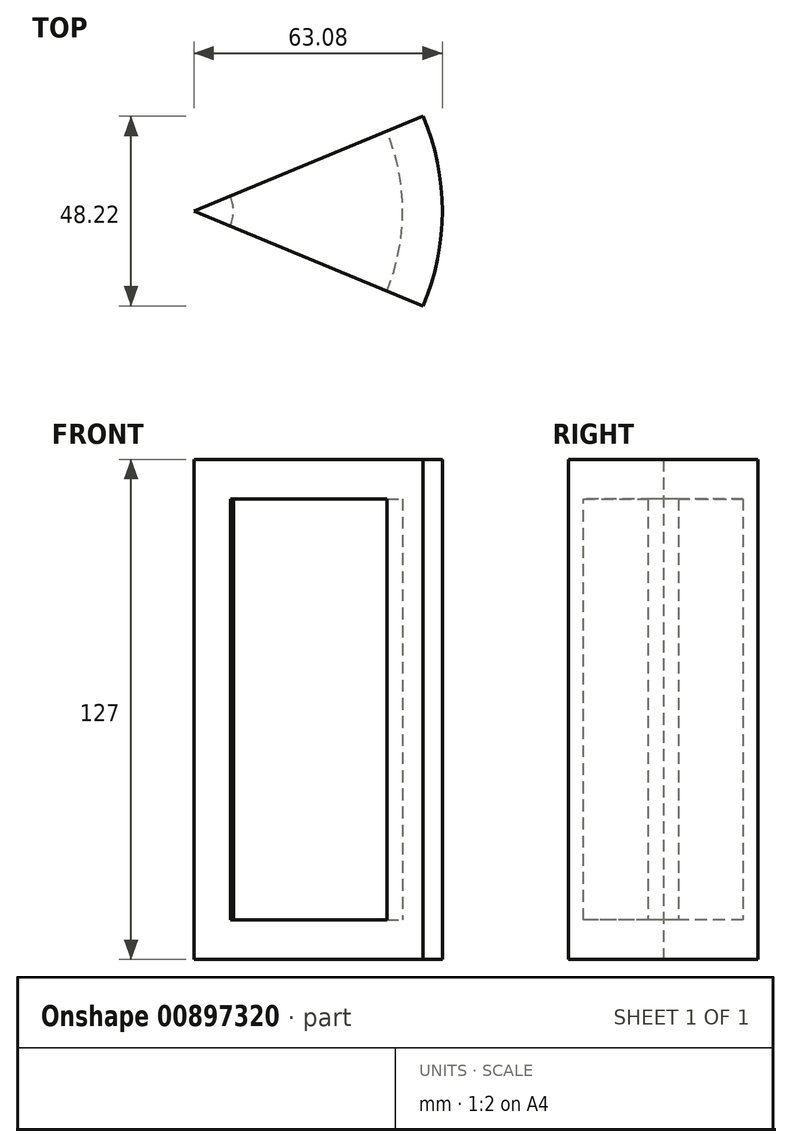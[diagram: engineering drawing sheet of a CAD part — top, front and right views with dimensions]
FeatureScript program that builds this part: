
annotation { "Feature Type Name" : "Feature", "Feature Type Description" : "" }
export const myFeature = defineFeature(function(context is Context, id is Id, definition is map)
    precondition{}
    {
        {
            var Q0;
            Q0=qCreatedBy(makeId("Top.planeOp"),FACE);
            var sketch = newSketch(context, id + "F0", { "sketchPlane" : qUnion([Q0])});
            skLineSegment(sketch, "E0", {"start": v(0, 0) * mm, "end": v(58.2, 24.1) * mm});
            skLineSegment(sketch, "E1", {"start": v(0, 0) * mm, "end": v(58.2, -24.1) * mm});
            skArc(sketch, "E2", {"start": v(58.2, -24.1) * mm, "mid": v(63.08, 0) * mm, "end": v(58.2, 24.1) * mm});
            skSolve(sketch);
        }
        {
            var Q0;
            Q0 = qSketchRegion(id + "F0", true);
            extrude(context, id + "F1", {"entities" : qUnion([Q0]), "depth" : 127 * mm, "offsetDistance" : 25 * mm});
        }
        {
            var Q0;
            Q0=makeQuery(id+"F1.opExtrude","SWEPT_FACE",FACE,{"disambiguationData":[OSD([sQuery(id+"F0.wireOp",EDGE,"E1")])]});
            var sketch = newSketch(context, id + "F2", { "sketchPlane" : qUnion([Q0])});
            skLineSegment(sketch, "E3.0", {"start": v(10, 10) * mm, "end": v(53, 10) * mm});
            skLineSegment(sketch, "E3.1", {"start": v(10, 117) * mm, "end": v(10, 10) * mm});
            skLineSegment(sketch, "E3.2", {"start": v(53, 117) * mm, "end": v(10, 117) * mm});
            skLineSegment(sketch, "E3.3", {"start": v(53, 10) * mm, "end": v(53, 117) * mm});
            skSolve(sketch);
        }
        {
            var Q0;
            Q0=makeQuery(id+"F2.imprint","IMPRINT",FACE,{"disambiguationData":[TD([[makeQuery(id+"F2.imprint","IMPRINT",EDGE,{"derivedFrom":sQuery(id+"F2.wireOp",EDGE,"E3.0")}),1.0]])]});
            var Q1;
            Q1=makeQuery(id+"F1.opExtrude","SWEPT_EDGE",EDGE,{"disambiguationData":[OSD([sQuery(id+"F0.wireOp",EDGE,"E0"),sQuery(id+"F0.wireOp",EDGE,"E1")])]});
            revolve(context, id + "F3", {"operationType" : NewBodyOperationType.REMOVE, "surfaceOperationType" : NewSurfaceOperationType.NEW, "entities" : qUnion([Q0]), "axis" : qUnion([Q1]), "revolveType" : RevolveType.ONE_DIRECTION, "oppositeDirection" : true, "angle" : 85 * degree});
        }
    });
